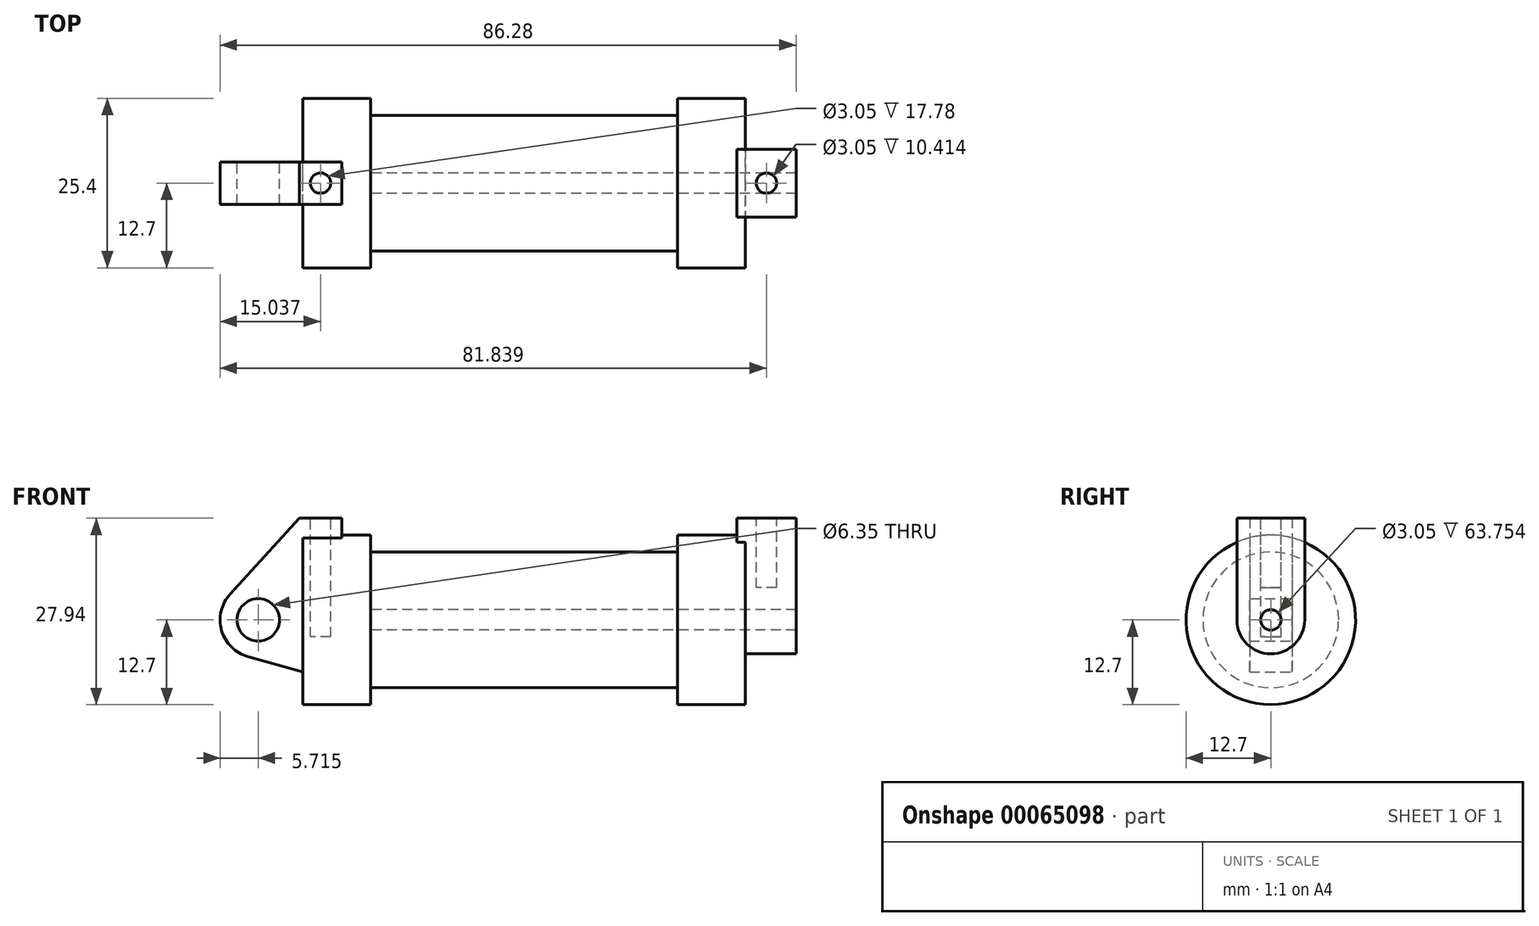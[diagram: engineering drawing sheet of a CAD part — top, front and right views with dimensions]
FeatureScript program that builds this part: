
annotation { "Feature Type Name" : "Feature", "Feature Type Description" : "" }
export const myFeature = defineFeature(function(context is Context, id is Id, definition is map)
    precondition{}
    {
        {
            var Q0;
            Q0=qCreatedBy(makeId("Front.planeOp"),FACE);
            var sketch = newSketch(context, id + "F0", { "sketchPlane" : qUnion([Q0])});
            skLineSegment(sketch, "E0", {"start": v(0, 0) * mm, "end": v(0, 12.7) * mm});
            skLineSegment(sketch, "E1", {"start": v(0, 12.7) * mm, "end": v(10.16, 12.7) * mm});
            skLineSegment(sketch, "E2", {"start": v(10.16, 12.7) * mm, "end": v(10.16, 10.16) * mm});
            skLineSegment(sketch, "E3", {"start": v(10.16, 10.16) * mm, "end": v(56.13, 10.16) * mm});
            skLineSegment(sketch, "E4", {"start": v(56.13, 10.16) * mm, "end": v(56.13, 12.7) * mm});
            skLineSegment(sketch, "E5", {"start": v(56.13, 12.7) * mm, "end": v(66.3, 12.7) * mm});
            skLineSegment(sketch, "E6", {"start": v(66.3, 12.7) * mm, "end": v(66.3, 0) * mm});
            skLineSegment(sketch, "E7", {"start": v(66.3, 0) * mm, "end": v(0, 0) * mm});
            skLineSegment(sketch, "E8", {"start": v(5.84, 15.24) * mm, "end": v(-0.5, 15.24) * mm});
            skLineSegment(sketch, "E9", {"start": v(-0.5, 15.24) * mm, "end": v(-10.88, 3.85) * mm});
            skLineSegment(sketch, "E10", {"start": v(0, 0) * mm, "end": v(-6.65, 0) * mm});
            skCircle(sketch, "E11", {"center": v(-6.65, 0) * mm, "radius": 5.72 * mm});
            skCircle(sketch, "E12", {"center": v(-6.65, 0) * mm, "radius": 3.18 * mm});
            skLineSegment(sketch, "E13", {"start": v(5.84, 15.24) * mm, "end": v(5.84, -9.4) * mm});
            skLineSegment(sketch, "E14", {"start": v(5.84, -9.4) * mm, "end": v(-8.18, -5.5) * mm});
            skSolve(sketch);
        }
        {
            var Q0;
            {var subQ0=sQuery(id+"F0.wireOp",EDGE,"E0");Q0=makeQuery(id+"F0.imprint","IMPRINT",FACE,{"disambiguationData":[TD([[makeQuery(id+"F0.imprint","IMPRINT",EDGE,{"derivedFrom":subQ0}),-1.0]])]});}
            var Q1;
            {var subQ0=sQuery(id+"F0.wireOp",EDGE,"E2");Q1=makeQuery(id+"F0.imprint","IMPRINT",FACE,{"disambiguationData":[TD([[makeQuery(id+"F0.imprint","IMPRINT",EDGE,{"derivedFrom":subQ0}),-1.0]])]});}
            var Q2;
            Q2=sQuery(id+"F0.wireOp",EDGE,"E10");
            revolve(context, id + "F1", {"entities" : qUnion([Q0, Q1]), "axis" : qUnion([Q2]), "revolveType" : RevolveType.FULL});
        }
        {
            var Q0;
            {var subQ3=sQuery(id+"F0.wireOp",EDGE,"E0");Q0=makeQuery(id+"F0.imprint","IMPRINT",FACE,{"disambiguationData":[TD([[makeQuery(id+"F0.imprint","IMPRINT",EDGE,{"derivedFrom":subQ3}),1.0]])]});}
            var Q1;
            {var subQ0=sQuery(id+"F0.wireOp",EDGE,"E14");Q1=makeQuery(id+"F0.imprint","IMPRINT",FACE,{"disambiguationData":[TD([[makeQuery(id+"F0.imprint","IMPRINT",EDGE,{"derivedFrom":subQ0}),-1.0]])]});}
            var Q2;
            {var subQ4=sQuery(id+"F0.wireOp",EDGE,"E12");Q2=makeQuery(id+"F0.imprint","IMPRINT",FACE,{"disambiguationData":[TD([[makeQuery(id+"F0.imprint","IMPRINT",EDGE,{"derivedFrom":subQ4}),-1.0]])]});}
            var Q3;
            {var subQ0=sQuery(id+"F0.wireOp",EDGE,"E0");Q3=makeQuery(id+"F0.imprint","IMPRINT",FACE,{"disambiguationData":[TD([[makeQuery(id+"F0.imprint","IMPRINT",EDGE,{"derivedFrom":subQ0}),-1.0]])]});}
            extrude(context, id + "F2", {"entities" : qUnion([Q0, Q1, Q2, Q3]), "operationType" : NewBodyOperationType.ADD, "endBound" : BoundingType.SYMMETRIC, "depth" : 6.35 * mm});
        }
        {
            var Q0;
            Q0=makeQuery(id+"F1.opRevolve","SWEPT_FACE",FACE,{"disambiguationData":[OSD([sQuery(id+"F0.wireOp",EDGE,"E6")])]});
            var sketch = newSketch(context, id + "F3", { "sketchPlane" : qUnion([Q0])});
            skCircle(sketch, "E15", {"center": v(0, 0) * mm, "radius": 1.52 * mm});
            skCircle(sketch, "E16", {"center": v(0, 0) * mm, "radius": 5.08 * mm});
            skLineSegment(sketch, "E17", {"start": v(-5.08, 0) * mm, "end": v(-5.08, 15.24) * mm});
            skLineSegment(sketch, "E18", {"start": v(5.08, 0) * mm, "end": v(5.08, 15.24) * mm});
            skLineSegment(sketch, "E19", {"start": v(5.08, 15.24) * mm, "end": v(-5.08, 15.24) * mm});
            skSolve(sketch);
        }
        {
            var Q0;
            {var subQ0=sQuery(id+"F3.wireOp",EDGE,"E17");var subQ1=sQuery(id+"F3.wireOp",EDGE,"E16");var subQ2=makeQuery(id+"F3.imprint","INTERSECT",VERTEX,{"derivedFrom":[subQ1,subQ0]});Q0=makeQuery(id+"F3.imprint","IMPRINT",FACE,{"disambiguationData":[TD([[makeQuery(id+"F3.imprint","IMPRINT",EDGE,{"disambiguationData":[TD([[subQ2,1.0]])],"derivedFrom":subQ1}),-1.0]])]});}
            var Q1;
            {var subQ0=sQuery(id+"F3.wireOp",EDGE,"E19");Q1=makeQuery(id+"F3.imprint","IMPRINT",FACE,{"disambiguationData":[TD([[makeQuery(id+"F3.imprint","IMPRINT",EDGE,{"derivedFrom":subQ0}),1.0]])]});}
            var Q2;
            Q2=makeQuery(id+"F3.imprint","IMPRINT",FACE,{"disambiguationData":[TD([[makeQuery(id+"F3.imprint","IMPRINT",EDGE,{"derivedFrom":sQuery(id+"F3.wireOp",EDGE,"E15")}),-1.0]])]});
            extrude(context, id + "F4", {"entities" : qUnion([Q0, Q1, Q2]), "operationType" : NewBodyOperationType.ADD, "depth" : 7.62 * mm, "hasSecondDirection" : true, "secondDirectionOppositeDirection" : true, "secondDirectionDepth" : 1.27 * mm});
        }
        {
            var Q0;
            Q0=makeQuery(id+"F4.boolean.opBoolean","SPLIT",FACE,{"disambiguationData":[TD([makeQuery(id+"F4.opExtrude","SWEPT_FACE",FACE,{"disambiguationData":[OSD([sQuery(id+"F3.wireOp",EDGE,"E15")])]})])],"derivedFrom":makeQuery(id+"F1.opRevolve","SWEPT_FACE",FACE,{"disambiguationData":[OSD([sQuery(id+"F0.wireOp",EDGE,"E6")])]})});
            var Q1;
            Q1=makeQuery(id+"F1.opRevolve","SWEPT_FACE",FACE,{"disambiguationData":[OSD([sQuery(id+"F0.wireOp",EDGE,"E2")])]});
            extrude(context, id + "F5", {"entities" : qUnion([Q0]), "operationType" : NewBodyOperationType.REMOVE, "endBound" : BoundingType.UP_TO_SURFACE, "oppositeDirection" : true, "endBoundEntityFace" : qUnion([Q1]), "depth" : 25.4 * mm});
        }
        {
            var Q0;
            Q0=makeQuery(id+"F2.opExtrude","SWEPT_FACE",FACE,{"disambiguationData":[OSD([sQuery(id+"F0.wireOp",EDGE,"E8")])]});
            var sketch = newSketch(context, id + "F6", { "sketchPlane" : qUnion([Q0])});
            skLineSegment(sketch, "E20", {"start": v(-0.5, 0) * mm, "end": v(5.84, 0) * mm, "construction": true});
            skLineSegment(sketch, "E21", {"start": v(2.67, 3.18) * mm, "end": v(2.67, -3.18) * mm, "construction": true});
            skCircle(sketch, "E22", {"center": v(2.67, 0) * mm, "radius": 1.52 * mm});
            skSolve(sketch);
        }
        {
            var Q0;
            Q0 = qSketchRegion(id + "F6", true);
            extrude(context, id + "F7", {"entities" : qUnion([Q0]), "operationType" : NewBodyOperationType.REMOVE, "oppositeDirection" : true, "depth" : 17.78 * mm});
        }
        {
            var Q0;
            Q0=makeQuery(id+"F4.opExtrude","SWEPT_FACE",FACE,{"disambiguationData":[OSD([sQuery(id+"F3.wireOp",EDGE,"E19")])]});
            var sketch = newSketch(context, id + "F8", { "sketchPlane" : qUnion([Q0])});
            skCircle(sketch, "E23", {"center": v(69.47, 0) * mm, "radius": 1.52 * mm});
            skPoint(sketch, "E23.centerSnap0", {"position": v(69.47, 5.08) * mm});
            skPoint(sketch, "E23.centerSnap1", {"position": v(73.91, 0) * mm});
            skSolve(sketch);
        }
        {
            var Q0;
            Q0 = qSketchRegion(id + "F8", true);
            extrude(context, id + "F9", {"entities" : qUnion([Q0]), "operationType" : NewBodyOperationType.REMOVE, "oppositeDirection" : true, "depth" : 10.4 * mm});
        }
    });
